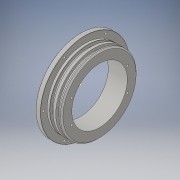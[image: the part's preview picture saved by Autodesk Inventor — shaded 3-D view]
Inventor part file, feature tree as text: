
AUTODESK INVENTOR PART (.ipt)
format: ipt  version: 2,016 (Build 200138000, 138)  size: 634,880 bytes
history: native  units: in
note: dims shown in document units (in); Inventor stores cm internally (conversion verified against a paired STEP export)
features: sketch x5, extrude x3, chamfer x2, revolve x1, hole x1
ambient origin geometry x8: Origin, YZ Plane, XZ Plane, XY Plane, X Axis, Y Axis, Z Axis, Center Point
bodies: Solid1 (feature_tree)
feature tree (12):
  revolve  "Revolution1"  [1 undecoded]
  extrude  "Extrusion1"  Depth=0.13in
  extrude  "Extrusion2"  Depth=0.24in
  chamfer  "Chamfer1"  Distance=0.24in
  hole  "Hole1"  [1 undecoded]
  chamfer  "Chamfer2"  Distance=0.125in
  sketch  "Sketch8"  dims[d22=0.139in d23=0.0in d32=0.07in d33=0.125in d34=45.0deg]
  extrude  "Extrusion4"  Depth=0.995in
  sketch  "Sketch2"  dims[d2=0.175in d3=0.14in]
  sketch  "Sketch3"  dims[d4=0.175in d5=0.13in]
  sketch  "Sketch5"  dims[d8=90.0deg d10=4.65in d11=0.24in d12=0.0in]
  sketch  "Sketch9"  dims[d38=0.5in d42=0.125in d43=4.35in d44=2.3622in d46=360.0deg d48=0.1181in d49=0.75in d50=0.375in d51=0.25in d52=0.5635in d53=1.0in d54=0.8108in d55=0.01in d56=0.125in d57=45.0deg d62=3.819in d65=0.15in d66=0.15in d67=0.15in d68=0.055in d71=0.755in d72=1.68in d73=0.3in d74=0.3in d78=0.1181in d79=0.1181in d83=0.1181in d84=0.1181in d85=0.995in d86=0.0in]
note: 2 required parameter values undecoded (feature->parameter linkage not recoverable at this tier; creation-order binding heuristic only, values carry confidence <= 0.55)